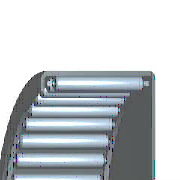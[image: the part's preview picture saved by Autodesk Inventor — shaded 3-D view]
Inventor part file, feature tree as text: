
AUTODESK INVENTOR PART (.ipt)
format: ipt  version: 2025.2 (Build 292293000, 293)  size: 289,792 bytes
history: native  units: mm (DEFAULTED — no unit token found)
features: other x3, pattern_circular x1
ambient origin geometry x8: Origin, YZ Plane, XZ Plane, XY Plane, X Axis, Y Axis, Z Axis, Center Point
bodies: Solid1 (feature_tree)
feature tree (4):
  other  "Körper"
  other  "Nut"
  other  "Rolle"
  pattern_circular  "Nuten"  Angle=90.0deg  [1 undecoded]
note: 1 required parameter value undecoded (feature->parameter linkage not recoverable at this tier; creation-order binding heuristic only, values carry confidence <= 0.55)
